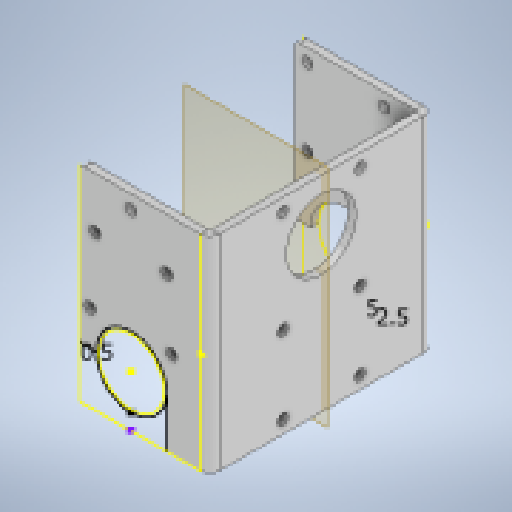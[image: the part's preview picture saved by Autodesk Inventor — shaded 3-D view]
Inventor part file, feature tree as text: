
AUTODESK INVENTOR PART (.ipt)
format: ipt  version: 2024.2 (Build 282272000, 272)  size: 250,880 bytes
history: native  units: in
note: dims shown in document units (in); Inventor stores cm internally (conversion verified against a paired STEP export)
features: reference x18, other x9, sketch x8, sheet_metal_op x4, hole x3, plane x1, chamfer x1
ambient origin geometry x8: Origin, YZ Plane, XZ Plane, XY Plane, X Axis, Y Axis, Z Axis, Center Point
bodies: Solid1 (feature_tree)
feature tree (44):
  sheet_metal_op  "Face1"
  sheet_metal_op  "Flange1"
  sketch  "Sketch3"  dims[d4=0.0295in d5=0.1181in]
  sketch  "Sketch4"  dims[d6=0.0122in]
  plane  "Work Plane1"
  hole  "Hole1"  [1 undecoded]
  sketch  "Sketch6"  dims[d10=0.2362in]
  chamfer  "Corner Round1"
  hole  "Hole2"  [1 undecoded]
  hole  "Hole3"  [1 undecoded]
  sketch  "Sketch1"  dims[d0=1.5787in d1=1.5945in]
  other  "Plate1"
  sketch  "Sketch2"  dims[d2=0.0591in d3=0.0591in]
  other  "Plate2"
  sheet_metal_op  "Bend1"
  sheet_metal_op  "Corner1"
  reference  "Reference1"
  sketch  "Sketch5"  dims[d7=1.0039in d8=90.0deg d9=0.0122in]
  reference  "Reference2"
  reference  "Reference3"
  reference  "Reference4"
  reference  "Reference5"
  reference  "Reference6"
  reference  "Reference7"
  reference  "Reference8"
  reference  "Reference9"
  reference  "Reference10"
  reference  "Reference11"
  sketch  "Sketch7"  dims[d11=0.0591in]
  reference  "Reference12"
  sketch  "Sketch8"  dims[d12=0.0122in d13=0.0197in d14=0.0591in d15=0.0in d16=0.0591in d17=0.0in d18=0.0827in d19=0.2362in d20=0.1575in d21=0.0787in d22=90.0deg d23=0.0591in d24=0.0in d25=0.0394in d26=0.0157in d27=0.0591in d28=0.0in d29=0.0827in d30=0.2362in d31=0.1575in d32=0.0787in d33=90.0deg d34=0.0591in d35=0.0in d36=0.0827in d37=0.2362in d38=0.1575in d39=0.0787in d40=90.0deg d41=0.0591in d42=0.0in d43=0.1969in d44=0.0984in d45=0.0246in]
  reference  "Reference13"
  reference  "Reference14"
  reference  "Reference15"
  reference  "Reference16"
  reference  "Reference17"
  reference  "Reference18"
  other  "Cut1"
  other  "Cut2"
  other  "Cut3"
  other  "2_Arm.iam"
  other  "HTD-45H:3"
  other  "HTD-45H:1"
  other  "HTD-45H:4"
note: 3 required parameter values undecoded (feature->parameter linkage not recoverable at this tier; creation-order binding heuristic only, values carry confidence <= 0.55)
